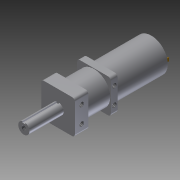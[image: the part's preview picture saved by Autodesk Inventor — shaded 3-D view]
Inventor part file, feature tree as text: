
AUTODESK INVENTOR PART (.ipt)
format: ipt  version: 2013 (Build 170138000, 138)  size: 205,312 bytes
history: native  units: in
note: dims shown in document units (in); Inventor stores cm internally (conversion verified against a paired STEP export)
features: sketch x10, extrude x8, fillet x3, hole x2, projected_geometry x2, plane x1, mirror x1
ambient origin geometry x8: Origin, YZ Plane, XZ Plane, XY Plane, X Axis, Y Axis, Z Axis, Center Point
bodies: Solid3 (feature_tree)
feature tree (27):
  extrude  "Extrusion2"  Depth=1.5in
  extrude  "Extrusion3"  Depth=1.45in
  extrude  "Extrusion4"  Depth=0.6in TaperAngle=0.0deg
  extrude  "Extrusion5"  Depth=0.125in
  hole  "Hole1"  [1 undecoded]
  plane  "Work Plane1"
  mirror  "Mirror1"
  hole  "Hole2"  [1 undecoded]
  extrude  "Extrusion6"  Depth=1.47in
  extrude  "Extrusion7"  Depth=0.15in
  extrude  "Extrusion8"  Depth=0.55in
  extrude  "Extrusion9"  Depth=0.55in
  fillet  "Fillet1"  Radius=0.215in
  fillet  "Fillet2"  Radius=0.5in
  fillet  "Fillet3"  Radius=0.16in
  sketch  "Sketch3"  dims[d4=1.5in d5=1.5in]
  sketch  "Sketch4"  dims[d6=0.3in d7=0.0in d8=1.45in]
  sketch  "Sketch5"  dims[d9=1.0in d10=0.0in d11=0.6in d12=0.0in]
  projected_geometry  "Projected Loop1"
  sketch  "Sketch6"  dims[d13=0.5in d14=0.125in]
  sketch  "Sketch7"  dims[d16=0.0625in d17=1.52in d18=0.0in]
  projected_geometry  "Projected Loop2"
  sketch  "Sketch8"  dims[d19=0.375in d20=0.375in]
  sketch  "Sketch9"  dims[d21=0.196in d22=0.3in d23=0.375in d24=0.25in d25=0.5635in d26=1.0in d27=0.8108in]
  sketch  "Sketch10"  dims[d28=0.196in d29=0.3in d30=0.375in d31=0.25in d32=0.5635in d33=1.0in d34=0.8108in d35=1.47in]
  sketch  "Sketch11"  dims[d36=2.25in d37=0.0in d38=0.15in]
  sketch  "Sketch12"  dims[d39=0.025in d40=0.55in d41=0.55in d42=0.215in d43=0.0in d44=0.5in d45=0.16in d46=0.0in d47=0.126in d48=0.05in d49=0.0in d50=0.0625in d51=0.0312in d52=0.125in]
note: 2 required parameter values undecoded (feature->parameter linkage not recoverable at this tier; creation-order binding heuristic only, values carry confidence <= 0.55)
